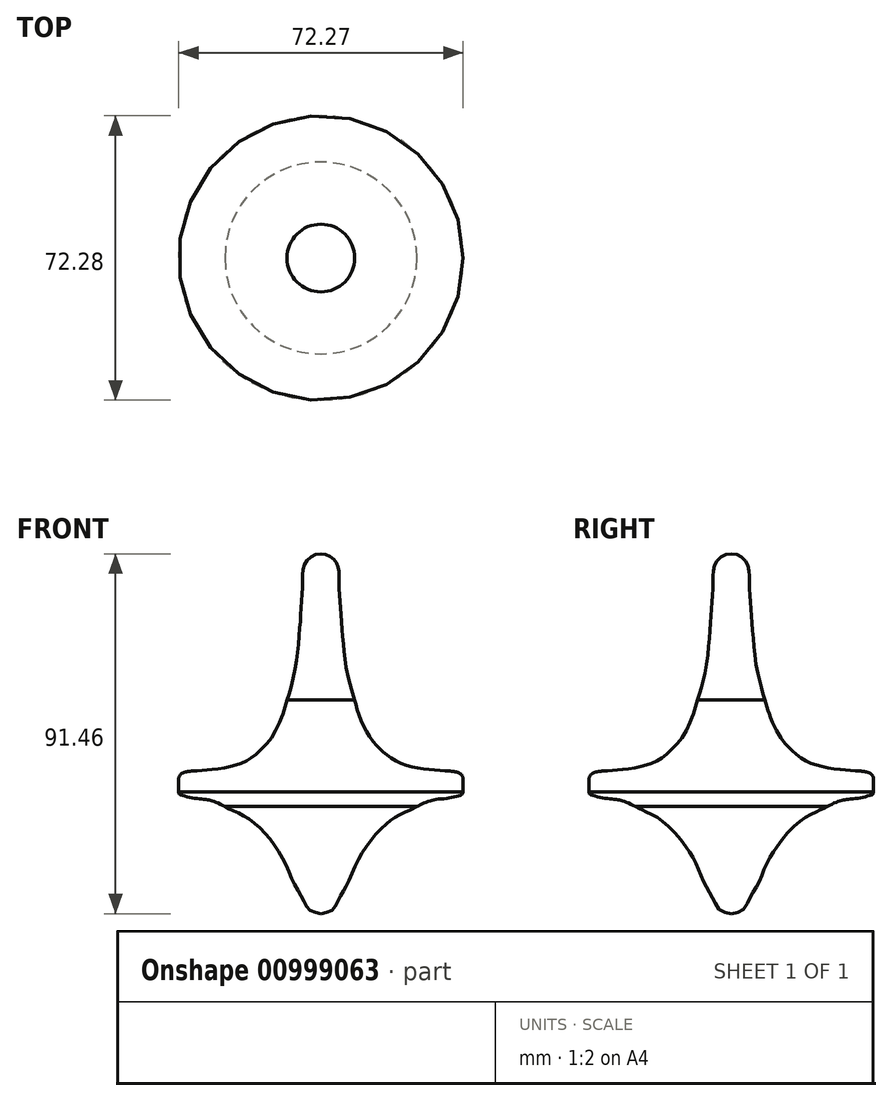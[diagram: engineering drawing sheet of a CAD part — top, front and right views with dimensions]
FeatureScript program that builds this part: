
annotation { "Feature Type Name" : "Feature", "Feature Type Description" : "" }
export const myFeature = defineFeature(function(context is Context, id is Id, definition is map)
    precondition{}
    {
        {
            var Q0;
            Q0=qCreatedBy(makeId("Front.planeOp"),FACE);
            var sketch = newSketch(context, id + "F0", { "sketchPlane" : qUnion([Q0])});
            skPoint(sketch, "E0.0.internal.snap0", {"position": v(-38, 73.46) * mm});
            skFitSpline(sketch, "E0", {"points": [v(-38, 72.72) * mm, v(-39.84, 72.32) * mm, v(-41.42, 71.18) * mm, v(-42.17, 69.96) * mm, v(-42.56, 68) * mm, v(-42.64, 65.56) * mm, v(-42.7, 62.77) * mm, v(-42.96, 59.33) * mm, v(-43.17, 56.19) * mm, v(-43.43, 53.05) * mm, v(-43.84, 48.36) * mm, v(-44.45, 43.72) * mm, v(-45.78, 38.1) * mm, v(-46.6, 35.6) * mm], "startDerivative": vector(-30.65, -3.4) * mm, "endDerivative": vector(-10.68, -30.26) * mm});
            skFitSpline(sketch, "E1", {"points": [v(-46.6, 35.6) * mm, v(-47.27, 33.08) * mm, v(-48.6, 29.59) * mm, v(-50.47, 26.16) * mm, v(-52.55, 23.56) * mm, v(-54.19, 22.07) * mm, v(-56.5, 20.36) * mm, v(-59.62, 19.02) * mm, v(-63.11, 18.2) * mm, v(-66.61, 17.83) * mm, v(-69.51, 17.6) * mm], "startDerivative": vector(-6.42, -26.77) * mm, "endDerivative": vector(-29.62, -2.24) * mm});
            skFitSpline(sketch, "E2", {"points": [v(-69.51, 17.6) * mm, v(-71.22, 17.47) * mm, v(-72.4, 17.27) * mm, v(-72.97, 17.08) * mm, v(-73.73, 16.57) * mm, v(-74.1, 15.84) * mm, v(-74.13, 15.28) * mm], "startDerivative": vector(-7.74, -0.51) * mm, "endDerivative": vector(0.01, -4.14) * mm});
            skLineSegment(sketch, "E3", {"start": v(-74.13, 15.28) * mm, "end": v(-74.13, 12.23) * mm});
            skFitSpline(sketch, "E4", {"points": [v(-74.13, 12.23) * mm, v(-73.88, 11.59) * mm, v(-73.1, 11.25) * mm, v(-71.38, 10.86) * mm, v(-69.5, 10.5) * mm, v(-67.26, 10.3) * mm, v(-66.08, 10.01) * mm, v(-64.64, 9.58) * mm, v(-63.29, 8.97) * mm, v(-62.39, 8.48) * mm], "startDerivative": vector(2.1, -9.15) * mm, "endDerivative": vector(8.88, -4.96) * mm});
            skFitSpline(sketch, "E5", {"points": [v(-62.39, 8.48) * mm, v(-60.15, 7.4) * mm, v(-57.34, 6) * mm, v(-53.44, 3.03) * mm, v(-49.85, -1.26) * mm, v(-46.79, -6.41) * mm, v(-44.78, -11.1) * mm, v(-42.67, -14.84) * mm, v(-40.96, -17.73) * mm, v(-38, -18.74) * mm], "startDerivative": vector(25.23, -12.47) * mm, "endDerivative": vector(29.81, -7.24) * mm});
            skLineSegment(sketch, "E6", {"start": v(-38, 73.46) * mm, "end": v(-38, -18.74) * mm});
            skSolve(sketch);
        }
        {
            var Q0;
            {var subQ0=sQuery(id+"F0.wireOp",EDGE,"E0");Q0=makeQuery(id+"F0.imprint","IMPRINT",FACE,{"disambiguationData":[TD([[makeQuery(id+"F0.imprint","IMPRINT",EDGE,{"derivedFrom":subQ0}),1.0]])]});}
            var Q1;
            Q1=sQuery(id+"F0.wireOp",EDGE,"E6");
            revolve(context, id + "F1", {"surfaceOperationType" : NewSurfaceOperationType.NEW, "entities" : qUnion([Q0]), "axis" : qUnion([Q1]), "revolveType" : RevolveType.FULL});
        }
    });
